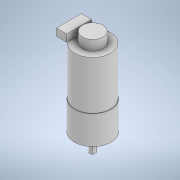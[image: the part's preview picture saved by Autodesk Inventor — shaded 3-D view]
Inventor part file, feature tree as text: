
AUTODESK INVENTOR PART (.ipt)
format: ipt  version: 2020.2 (Build 242310000, 310)  size: 182,272 bytes
history: native  units: mm
features: sketch x10, extrude x8, hole x1
ambient origin geometry x8: Origin, YZ Plane, XZ Plane, XY Plane, X Axis, Y Axis, Z Axis, Center Point
bodies: Solido1 (feature_tree)
feature tree (19):
  extrude  "Estrusione1"  Depth=24.4mm
  extrude  "Estrusione2"  Depth=31.0mm TaperAngle=0.0deg
  extrude  "Estrusione3"  Depth=25.0mm
  extrude  "Estrusione4"  Depth=19.5mm TaperAngle=0.0deg
  extrude  "Estrusione5"  Depth=7.0mm
  hole  "Foro1"  [1 undecoded]
  sketch  "Schizzo7"
  extrude  "Estrusione6"  Depth=4.0mm
  extrude  "Estrusione7"  Depth=9.5mm TaperAngle=0.0deg
  extrude  "Estrusione8"  Depth=3.5mm
  sketch  "Schizzo1"
  sketch  "Schizzo2"
  sketch  "Schizzo3"
  sketch  "Schizzo4"
  sketch  "Schizzo5"
  sketch  "Schizzo6"
  sketch  "Schizzo8"
  sketch  "Schizzo9"
  sketch  "Schizzo10"
note: 1 required parameter value undecoded (feature->parameter linkage not recoverable at this tier; creation-order binding heuristic only, values carry confidence <= 0.55)
